# Revit family: Resan WC Pan V2 - Wall Fixing
name_source: partatom
category: Plumbing Fixtures
revit_build: Autodesk Revit 2017 (Build: 20160225_1515(x64)
units: mm (PartAtom-declared; Revit-internal decimal feet)

## family parameters
Cut with Voids When Loaded = No
Host = Face
Part Type = Normal
Room Calculation Point = No
Round Connector Dimension = Use Diameter
Shared = No

## types (4) — shared parameters
Anti-Vandal = Yes
CE Approval = Yes
Colour = White
Coverage Area = 0.084m^3
Default Elevation = 1219 mm
EAN Number = -
Features = Anti-Vandal
Flush Type = Single / Dual Flush
Flush Volumes = 6L single flush; 6/4L, 5/3L, 4/2.6L dual flush
Gross Weight = 50KG
Inlet Diameter = 43.5mm
Installation Type = Wall
Issue = 1
Maintenance Instructions = Refer to instructions
Manufacturer = Thomas Dudley Ltd
Manufacturer Country = UK
Material = Polyester Resin
Model = Resan WC Pan V2
Optional Peripherals = Dudley Miniflo, pushbuttons & pushplates range, Dudley Electroflo
Outlet Diameter = 100mm / 4" Soil Pipe
Overall Height = 415 mm  [stored 1.36155 ft]
Overall Length = 498 mm  [stored 1.63386 ft]
Overall Width = 394 mm
Product Instructions = http://www.thomasdudley.co.uk
Product Literature = http://www.dudleyresan.co.uk
Product Range = Resan
Publish Date = 02/10/2019
Reference Standard = BS EN 997:2012+A1:2015 / Water Fittings Regulations
Servicing = Refer to instructions
Shipping Weight = 52KG
Spares = http://spares.thomasdudley.co.uk
Type = WC Pan
URL = http://www.dudleyresan.co.uk
Warranty = 5 Year
Warranty Type = Parts
YouTube Link = https://www.youtube.com
zero-valued in all types: Access Clearance Bottom, Access Clearance Front, Access Clearance Left, Access Clearance Rear, Access Clearance Right, Access Clearance Top

## per-type parameters (varying)
| type | Finish | Mandatory Requirements | Material Finish | Product Code | Toilet Seat |
| 333987 WC Pan V2 - BTW - Matt Finish | Stonecast Matt |  | Stonecast Matt White | PRESWC333987 | No |
| 333986 WC Pan V2 - BTW - Polished Gloss Finish | Polished Gloss |  | Polished Gloss White | PRESWC333986 | No |
| 334069 WC Pan V2 - BTW - Matt Finish - With Toilet Seat | Stonecast Matt | 320725 Eve seat & 320913 Top fix hinge (C33) | Stonecast Matt White | PRESWC334069 | Yes |
| 334070 WC Pan V2 - BTW - Polished Gloss Finish - With Toilet Seat | Polished Gloss | 320725 Eve seat & 320913 Top fix hinge (C33) | Polished Gloss White | PRESWC334070 | Yes |

note: [stored X ft] marks values corroborated as IEEE doubles in the binary element streams (Revit-internal decimal feet)

## geometry (parser evidence)
native form markers: Sweep x2
no freeform markers — native parametric forms only
